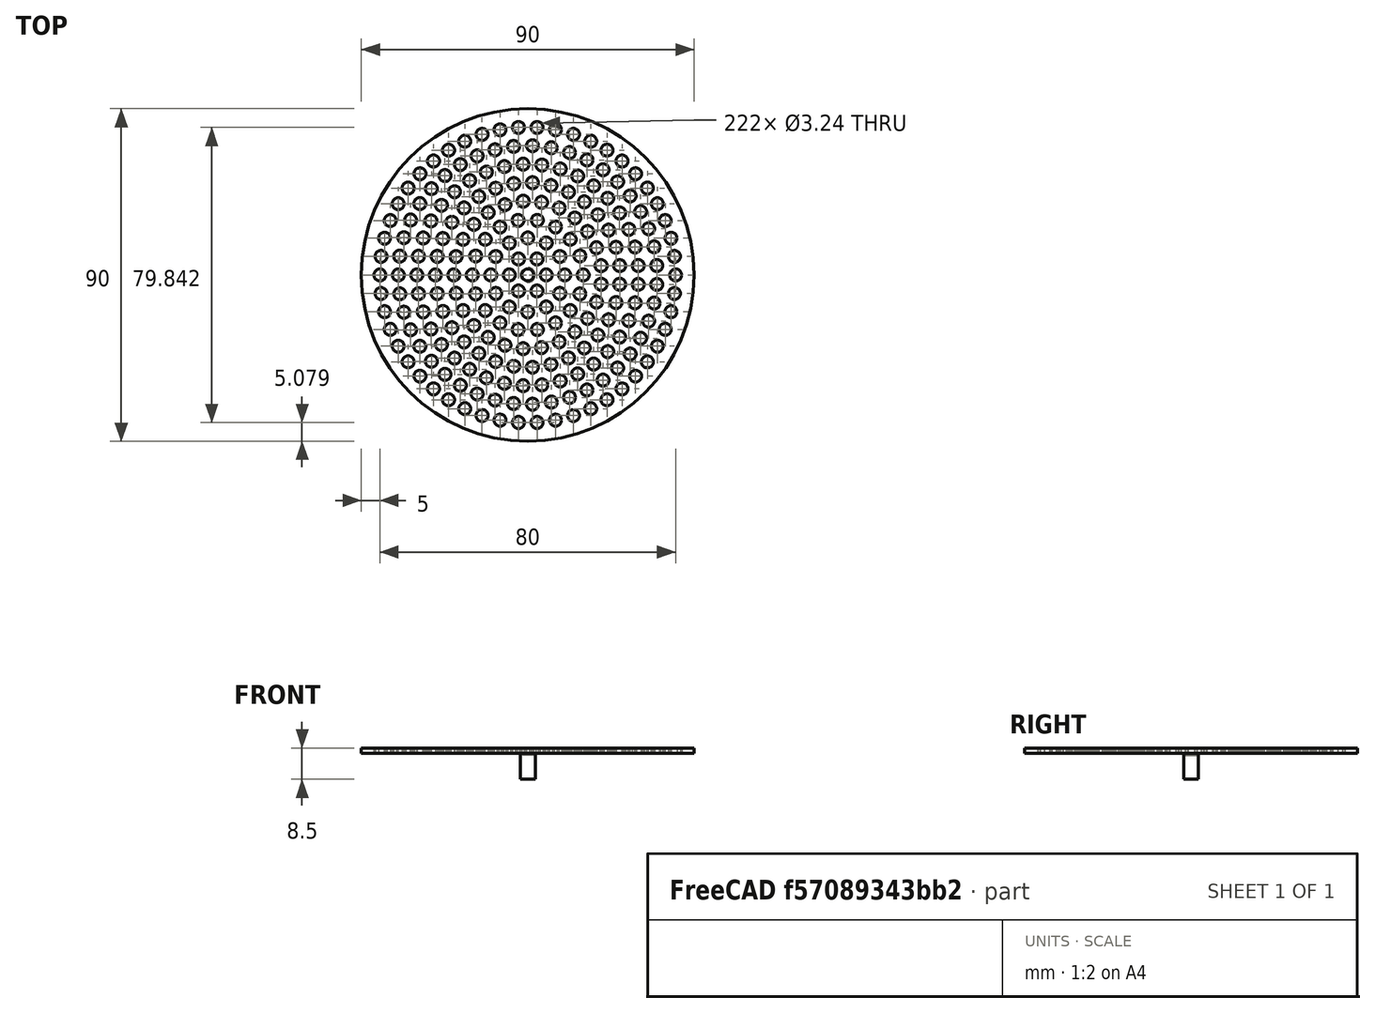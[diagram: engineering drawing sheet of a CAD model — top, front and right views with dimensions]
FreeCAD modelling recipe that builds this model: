
FCSTD DOCUMENT  (FreeCAD 0.20R)
Label: PhilippsXL30_SampleMountAdapter_Breadboard
License: All rights reserved
LicenseURL: http://en.wikipedia.org/wiki/All_rights_reserved
objects: TechDraw::DrawViewDimension×5, Part::Cylinder×3, Part::FeaturePython×3, TechDraw::DrawProjGroupItem×3, Part::Cut×2, Part::MultiFuse×2, Spreadsheet::Sheet×1, TechDraw::DrawSVGTemplate×1, TechDraw::DrawProjGroup×1, TechDraw::DrawViewAnnotation×1, TechDraw::DrawPage×1
note: 9 computed .brp shape members not serialized (recipe doc carries the construction recipe); baked Part::Feature solids carry a one-line shape summary decoded from their .brp

FEATURE [Spreadsheet::Sheet] Spreadsheet  label="StageParameters"
  cells = A1=Model parameters; A2=Stage diameter; B2(stagediameter)=90; C2=Keep in mind this might limit the movement area; A3=Stage thickness; B3(stagethicknes)=1.5; C3=Thickness of the stage. Should be at least one threading step; A4=Threading (metric); B4(threadingm)=4; C4=M3 or M4 threads; A5=Threading pitch; B5(threadingpitch)=0.7; C5=Should match the major diameter (M4: 0.7mm, M3: 0.5mm, etc.); A6=Lattice spacing; B6(threadingspacing)=5
FEATURE [Part::Cylinder] Cylinder
  Angle = 360
  AttacherType = Attacher::AttachEngine3D
  FirstAngle = 0
  Height = 1.5
  Radius = 45
  SecondAngle = 0
  expr: Height = <<StageParameters>>.stagethicknes
  expr: Radius = <<StageParameters>>.stagediameter / 2
FEATURE [Part::FeaturePython] ScrewTap  label="4x2-ScrewTap"  # Fasteners workbench fastener (typed FeaturePython)
  Placement = pos=(0,0,1.5) rot=(0,0,1;0rad)
  diameter = 29
  diameterCustom = 4
  invert = false
  leftHanded = false
  length = 2
  matchOuter = false
  offset = 0
  pitchCustom = 0.7
  thread = false
  type = 2
  expr: .Placement.Base.z = <<StageParameters>>.stagethicknes
  expr: diameterCustom = <<StageParameters>>.threadingm
  expr: length = <<StageParameters>>.stagethicknes
  expr: pitchCustom = <<StageParameters>>.threadingpitch
FEATURE [Part::FeaturePython] Array  # Draft array (typed FeaturePython)
  AlwaysSyncPlacement = false
  Angle = 360
  ArrayType = 2
  Axis = (0,0,1)
  Base = -> ScrewTap
  Center = (0,0,0)
  Count = 223
  ExpandArray = false
  Fuse = false
  IntervalAxis = (0,0,0)
  IntervalX = (50,0,0)
  IntervalY = (0,50,0)
  IntervalZ = (0,0,50)
  NumberCircles = 9
  NumberPolar = 5
  NumberX = 2
  NumberY = 2
  NumberZ = 1
  PlacementList = 223 placements: [(0,0,1.5),(-5,0,1.5),(-2.5,-4.33013,1.5),(2.5,-4.33013,1.5),(5,-6.12323e-16,1.5),(2.5,4.33013,1.5),(-2.5,4.33013,1.5),(-10,0,1.5),(-8.66025,-5,1.5),(-5,-8.66025,1.5),(-1.77636e-15,-10,1.5),(5,-8.66025,1.5),(8.66025,-5,1.5),(10,-1.22465e-15,1.5),(8.66025,5,1.5),(5,8.66025,1.5),(1.77636e-15,10,1.5),(-5,8.66025,1.5),(-8.66025,5,1.5),(-15,0,1.5),(-14.0954,-5.1303,1.5),(-11.4907,-9.64181,1.5),+201 more]
  RadialDistance = 5
  ScaleList = (223) [(1,1,1),(1,1,1),(1,1,1),(1,1,1),(1,1,1),(1,1,1),(1,1,1),(1,1,1),(1,1,1),(1,1,1),(1,1,1),(1,1,1),(1,1,1),(1,1,1),(1,1,1),(1,1,1),(1,1,1),(1,1,1),+205 more]
  Symmetry = 1
  TangentialDistance = 5
  expr: NumberCircles = <<StageParameters>>.stagediameter / 2 / <<StageParameters>>.threadingspacing
  expr: RadialDistance = <<StageParameters>>.threadingspacing
  expr: TangentialDistance = <<StageParameters>>.threadingspacing
FEATURE [Part::Cut] Cut
  Base = -> Cylinder
  Tool = -> Array
FEATURE [Part::Cylinder] Cylinder001
  Angle = 360
  AttacherType = Attacher::AttachEngine3D
  FirstAngle = 0
  Height = 1.5
  Radius = 2.1
  SecondAngle = 0
  expr: Height = <<StageParameters>>.stagethicknes
  expr: Radius = <<StageParameters>>.threadingm / 2 + 0.1
FEATURE [Part::MultiFuse] Fusion
  Shapes = -> [Cut,Cylinder001]
FEATURE [Part::Cylinder] Cylinder002
  Angle = 360
  AttacherType = Attacher::AttachEngine3D
  FirstAngle = 0
  Height = 7
  Placement = pos=(0,0,-7) rot=(0,0,1;0rad)
  Radius = 2
  SecondAngle = 0
FEATURE [Part::FeaturePython] ScrewTap001  label="M4x20-ScrewTap"  # Fasteners workbench fastener (typed FeaturePython)
  diameter = 6
  diameterCustom = 6
  invert = false
  leftHanded = false
  length = 20
  matchOuter = false
  offset = 0
  pitchCustom = 1
  thread = false
  type = 0
FEATURE [Part::Cut] Cut001
  Base = -> Cylinder002
  Tool = -> ScrewTap001
FEATURE [Part::MultiFuse] Fusion001  label="BreadboardStage"
  Shapes = -> [Fusion,Cut001]
FEATURE [TechDraw::DrawSVGTemplate] Template
  EditableTexts = Designed_by_Name=Thomas Spielauer; FC-Date=2023-12-20; FC-SC=mm; FC-Title=XL30 sample breadboard; Subtitle=Simple breadboard (M4 taps) for XL30 stage
  Height = 210
  Orientation = 1
  Width = 297
FEATURE [TechDraw::DrawProjGroupItem] ProjItem  label="Front"
  CoarseView = false
  Direction = (0,0,1)
  Focus = 100
  HardHidden = false
  IsoCount = 0
  IsoHidden = false
  IsoVisible = false
  LockPosition = true
  Perspective = false
  Rotation = 0
  RotationVector = (0,1,0)
  ScaleType = 2
  SeamHidden = false
  SeamVisible = true
  SmoothHidden = false
  SmoothVisible = true
  Source = -> [Fusion001]
  Type = 0
  X = 0
  XDirection = (0,1,0)
  Y = 0
FEATURE [TechDraw::DrawProjGroupItem] ProjItem002  label="Rear"
  CoarseView = false
  Direction = (0,0,-1)
  Focus = 100
  HardHidden = false
  IsoCount = 0
  IsoHidden = false
  IsoVisible = false
  LockPosition = false
  Perspective = false
  Rotation = 0
  RotationVector = (1,0,0)
  ScaleType = 2
  SeamHidden = false
  SeamVisible = true
  SmoothHidden = false
  SmoothVisible = true
  Source = -> [Fusion001]
  Type = 3
  X = 132.614
  XDirection = (0,-1,0)
  Y = 0
FEATURE [TechDraw::DrawProjGroupItem] ProjItem003  label="Bottom"
  CoarseView = false
  Direction = (1,0,0)
  Focus = 100
  HardHidden = false
  IsoCount = 0
  IsoHidden = false
  IsoVisible = false
  LockPosition = false
  Perspective = false
  Rotation = 0
  RotationVector = (1,0,0)
  ScaleType = 2
  SeamHidden = false
  SeamVisible = true
  SmoothHidden = false
  SmoothVisible = true
  Source = -> [Fusion001]
  Type = 5
  X = 0
  XDirection = (0,1,0)
  Y = -101.741
FEATURE [TechDraw::DrawProjGroup] ProjGroup
  Anchor = -> ProjItem
  AutoDistribute = false
  LockPosition = false
  ProjectionType = 0
  Rotation = 0
  ScaleType = 0
  Source = -> [Fusion001]
  Views = -> [ProjItem,ProjItem002,ProjItem003]
  X = 78.2727
  Y = 137.727
  spacingX = 15
  spacingY = 15
FEATURE [TechDraw::DrawViewDimension] Dimension
  AngleOverride = false
  Arbitrary = false
  ArbitraryTolerances = false
  EqualTolerance = true
  ExtensionAngle = 0
  FormatSpec = ⌀%.2w
  FormatSpecOverTolerance = %+.2w
  FormatSpecUnderTolerance = %+.2w
  Inverted = false
  LineAngle = 0
  LockPosition = false
  MeasureType = 1
  OverTolerance = 0
  References2D = -> [ProjItem]
  Rotation = 0
  ScaleType = 0
  TheoreticalExact = false
  Type = 5
  UnderTolerance = 0
  X = 60.5836
  Y = 19.2938
FEATURE [TechDraw::DrawViewDimension] Dimension001
  AngleOverride = false
  Arbitrary = false
  ArbitraryTolerances = false
  EqualTolerance = true
  ExtensionAngle = 0
  FormatSpec = %.2w
  FormatSpecOverTolerance = %+.2w
  FormatSpecUnderTolerance = %+.2w
  Inverted = false
  LineAngle = 0
  LockPosition = false
  MeasureType = 1
  OverTolerance = 0
  References2D = -> [ProjItem003]
  Rotation = 0
  ScaleType = 0
  TheoreticalExact = false
  Type = 0
  UnderTolerance = 0
  X = 55.6534
  Y = 12.8649
FEATURE [TechDraw::DrawViewDimension] Dimension002
  AngleOverride = false
  Arbitrary = false
  ArbitraryTolerances = false
  EqualTolerance = true
  ExtensionAngle = 0
  FormatSpec = %.2w
  FormatSpecOverTolerance = %+.2w
  FormatSpecUnderTolerance = %+.2w
  Inverted = false
  LineAngle = 0
  LockPosition = false
  MeasureType = 1
  OverTolerance = 0
  References2D = -> [ProjItem003]
  Rotation = 0
  ScaleType = 0
  TheoreticalExact = false
  Type = 0
  UnderTolerance = 0
  X = 58.9935
  Y = -4.00483
FEATURE [TechDraw::DrawViewDimension] Dimension003
  AngleOverride = false
  Arbitrary = false
  ArbitraryTolerances = false
  EqualTolerance = true
  ExtensionAngle = 0
  FormatSpec = %.2w (M4 threading)
  FormatSpecOverTolerance = %+.2w
  FormatSpecUnderTolerance = %+.2w
  Inverted = false
  LineAngle = 0
  LockPosition = false
  MeasureType = 1
  OverTolerance = 0
  References2D = -> [ProjItem003]
  Rotation = 0
  ScaleType = 0
  TheoreticalExact = false
  Type = 0
  UnderTolerance = 0
  X = 23.9628
  Y = -17.7735
FEATURE [TechDraw::DrawViewDimension] Dimension004
  AngleOverride = false
  Arbitrary = false
  ArbitraryTolerances = false
  EqualTolerance = true
  ExtensionAngle = 0
  FormatSpec = ⌀%.2w (M4 tap)
  FormatSpecOverTolerance = %+.2w
  FormatSpecUnderTolerance = %+.2w
  Inverted = false
  LineAngle = 0
  LockPosition = false
  MeasureType = 1
  OverTolerance = 0
  References2D = -> [ProjItem]
  Rotation = 0
  ScaleType = 0
  TheoreticalExact = false
  Type = 5
  UnderTolerance = 0
  X = 51.0782
  Y = 36.3539
FEATURE [TechDraw::DrawViewAnnotation] Annotation
  Font = osifont
  LineSpace = 80
  LockPosition = false
  MaxWidth = -1
  Rotation = 0
  ScaleType = 0
  Text = Spacing between bolt circles: 5mm | Spacing between holes: 5mm
  TextSize = 5
  TextStyle = 0
  X = 80.1989
  Y = 75.6429
FEATURE [TechDraw::DrawPage] Page
  KeepUpdated = true
  NextBalloonIndex = 1
  ProjectionType = 0
  Template = -> Template
  Views = -> [ProjGroup,Dimension,Dimension001,Dimension002,Dimension003,Dimension004,Annotation]
